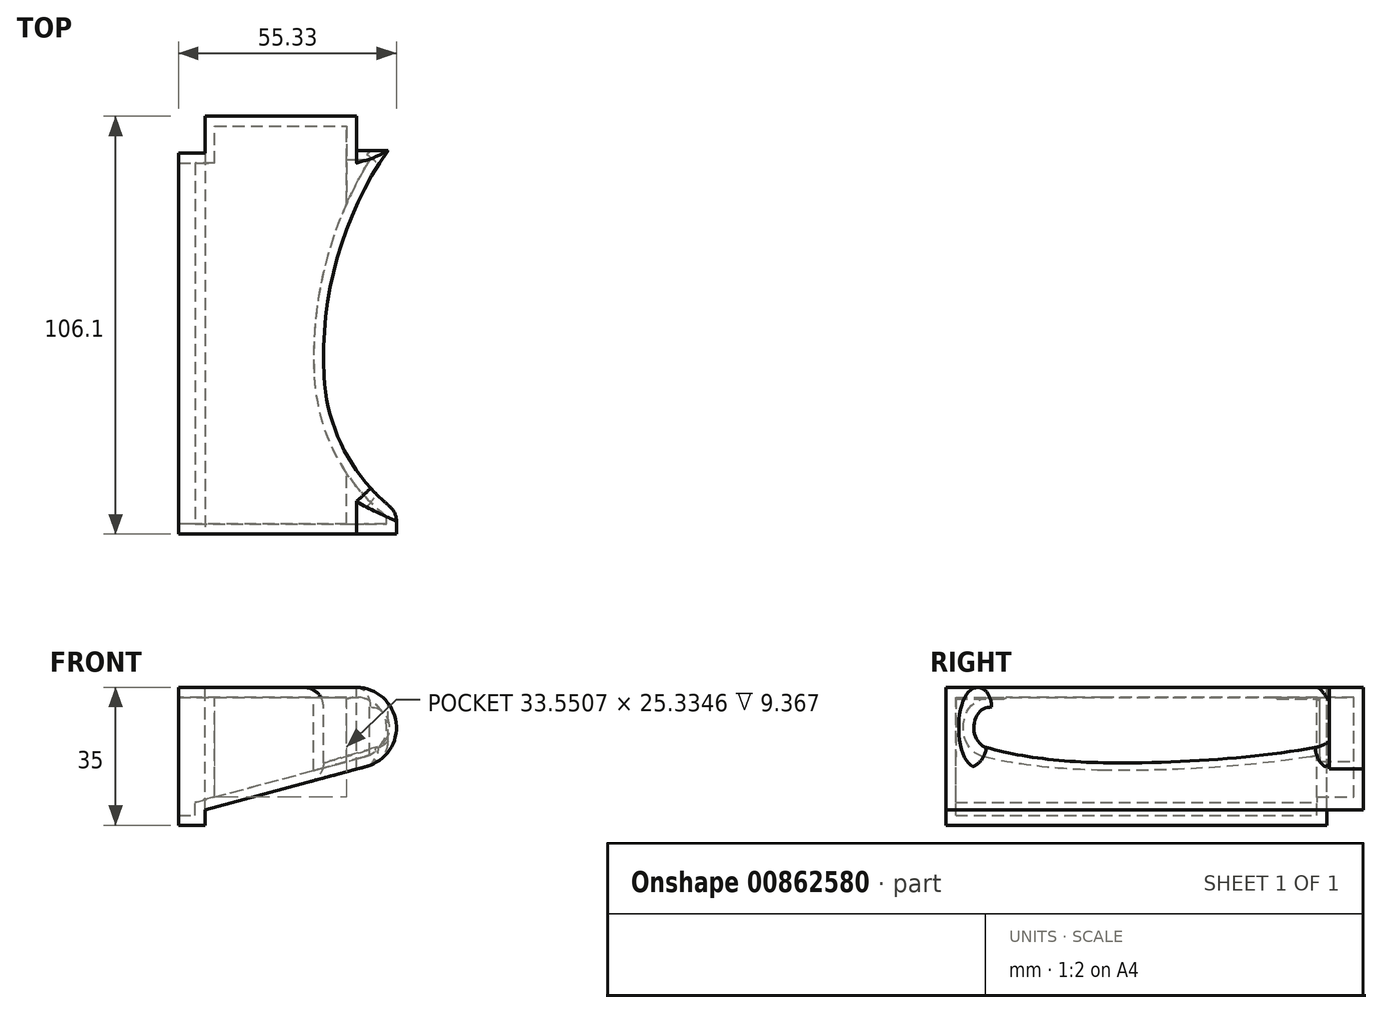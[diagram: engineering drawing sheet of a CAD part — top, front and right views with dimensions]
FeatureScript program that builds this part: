
annotation { "Feature Type Name" : "Feature", "Feature Type Description" : "" }
export const myFeature = defineFeature(function(context is Context, id is Id, definition is map)
    precondition{}
    {
        {
            var Q0;
            Q0=qCreatedBy(makeId("Top.planeOp"),FACE);
            var sketch = newSketch(context, id + "F0", { "sketchPlane" : qUnion([Q0])});
            skLineSegment(sketch, "E0", {"start": v(0, 0) * mm, "end": v(0, 96.74) * mm});
            skLineSegment(sketch, "E1", {"start": v(0, 96.74) * mm, "end": v(6.67, 96.74) * mm});
            skLineSegment(sketch, "E2", {"start": v(6.67, 96.74) * mm, "end": v(6.67, 106.1) * mm});
            skLineSegment(sketch, "E3", {"start": v(6.67, 106.1) * mm, "end": v(45.22, 106.1) * mm});
            skLineSegment(sketch, "E4", {"start": v(45.22, 106.1) * mm, "end": v(45.22, 97.46) * mm});
            skLineSegment(sketch, "E5", {"start": v(45.22, 97.46) * mm, "end": v(53.14, 97.46) * mm});
            skLineSegment(sketch, "E6", {"start": v(57.13, 0) * mm, "end": v(0, 0) * mm});
            skArc(sketch, "E7", {"start": v(36.93, 40.04) * mm, "mid": v(43.16, 19.28) * mm, "end": v(58.2, 3.69) * mm});
            skArc(sketch, "E8", {"start": v(53.14, 97.46) * mm, "mid": v(40.27, 70.1) * mm, "end": v(36.93, 40.04) * mm});
            skPoint(sketch, "E9.visualSharp", {"position": v(65.32, 0) * mm});
            skArc(sketch, "E10.filletArc", {"start": v(57.13, 0) * mm, "mid": v(59.05, 1.44) * mm, "end": v(58.2, 3.69) * mm});
            skSolve(sketch);
        }
        {
            var Q0;
            Q0=makeQuery(id+"F0.imprint","IMPRINT",FACE,{"disambiguationData":[TD([[makeQuery(id+"F0.imprint","IMPRINT",EDGE,{"derivedFrom":sQuery(id+"F0.wireOp",EDGE,"E0")}),-1.0]])]});
            extrude(context, id + "F1", {"entities" : qUnion([Q0]), "oppositeDirection" : true, "depth" : 35 * mm, "offsetDistance" : 25 * mm});
        }
        {
            var Q0;
            Q0=makeQuery(id+"F1.opExtrude","SWEPT_FACE",FACE,{"disambiguationData":[OSD([sQuery(id+"F0.wireOp",EDGE,"E3")])]});
            var sketch = newSketch(context, id + "F2", { "sketchPlane" : qUnion([Q0])});
            skLineSegment(sketch, "E11", {"start": v(-6.67, -35) * mm, "end": v(-6.67, -31.1) * mm});
            skLineSegment(sketch, "E12", {"start": v(-6.67, -31.1) * mm, "end": v(-47.76, -20.08) * mm});
            skLineSegment(sketch, "E13", {"start": v(-45.12, 0) * mm, "end": v(-6.67, 0) * mm});
            skLineSegment(sketch, "E14", {"start": v(-6.67, 0) * mm, "end": v(-6.67, 10.57) * mm});
            skLineSegment(sketch, "E15", {"start": v(-6.67, 10.57) * mm, "end": v(-70.74, 10.57) * mm});
            skLineSegment(sketch, "E16", {"start": v(-70.74, 10.57) * mm, "end": v(-70.74, -42.08) * mm});
            skLineSegment(sketch, "E17", {"start": v(-70.74, -42.08) * mm, "end": v(-6.67, -42.08) * mm});
            skLineSegment(sketch, "E18", {"start": v(-6.67, -42.08) * mm, "end": v(-6.67, -31.1) * mm});
            skArc(sketch, "E19", {"start": v(-45.12, 0) * mm, "mid": v(-55.24, -8.88) * mm, "end": v(-47.76, -20.08) * mm});
            skPoint(sketch, "E20.orphan", {"position": v(-59.18, 0) * mm});
            skSolve(sketch);
        }
        {
            var Q0;
            {var subQ11=sQuery(id+"F2.wireOp",EDGE,"E13");Q0=makeQuery(id+"F2.imprint","IMPRINT",FACE,{"disambiguationData":[TD([[makeQuery(id+"F2.imprint","IMPRINT",EDGE,{"derivedFrom":subQ11}),-1.0]])]});}
            var Q1;
            {var subQ2=sQuery(id+"F0.wireOp",EDGE,"E3");var subQ6=makeQuery(id+"F1.opExtrude","CAP_EDGE",EDGE,{"disambiguationData":[OSD([subQ2])],"isStart":false});Q1=makeQuery(id+"F2.imprint","IMPRINT",FACE,{"disambiguationData":[TD([[makeQuery(id+"F2.imprint","IMPRINT",EDGE,{"derivedFrom":subQ6}),-1.0]])]});}
            extrude(context, id + "F3", {"entities" : qUnion([Q0, Q1]), "operationType" : NewBodyOperationType.REMOVE, "oppositeDirection" : true, "depth" : 173.1 * mm, "offsetDistance" : 25 * mm});
        }
        {
            var Q0;
            Q0=makeQuery(id+"F1.opExtrude","SWEPT_FACE",FACE,{"disambiguationData":[OSD([sQuery(id+"F0.wireOp",EDGE,"E0")])]});
            shell(context, id + "F4", {"entities" : qUnion([Q0]), "thickness" : 2.5 * mm});
        }
        {
            var Q0;
            Q0=makeQuery(id+"F1.opExtrude","CAP_EDGE",EDGE,{"disambiguationData":[OSD([sQuery(id+"F0.wireOp",EDGE,"E7")])],"isStart":true});
            var Q1;
            Q1=makeQuery(id+"F3.boolean.opBoolean","INTERSECT",EDGE,{"derivedFrom":[makeQuery(id+"F1.opExtrude","SWEPT_FACE",FACE,{"disambiguationData":[OSD([sQuery(id+"F0.wireOp",EDGE,"E7")])]}),makeQuery(id+"F3.opExtrude","SWEPT_FACE",FACE,{"disambiguationData":[OSD([sQuery(id+"F2.wireOp",EDGE,"E12")])]})]});
            fillet(context, id + "F5", {"entities" : qUnion([Q0, Q1]), "radius" : 5 * mm, "tangentPropagation" : true, "allowEdgeOverflow" : false});
        }
    });
